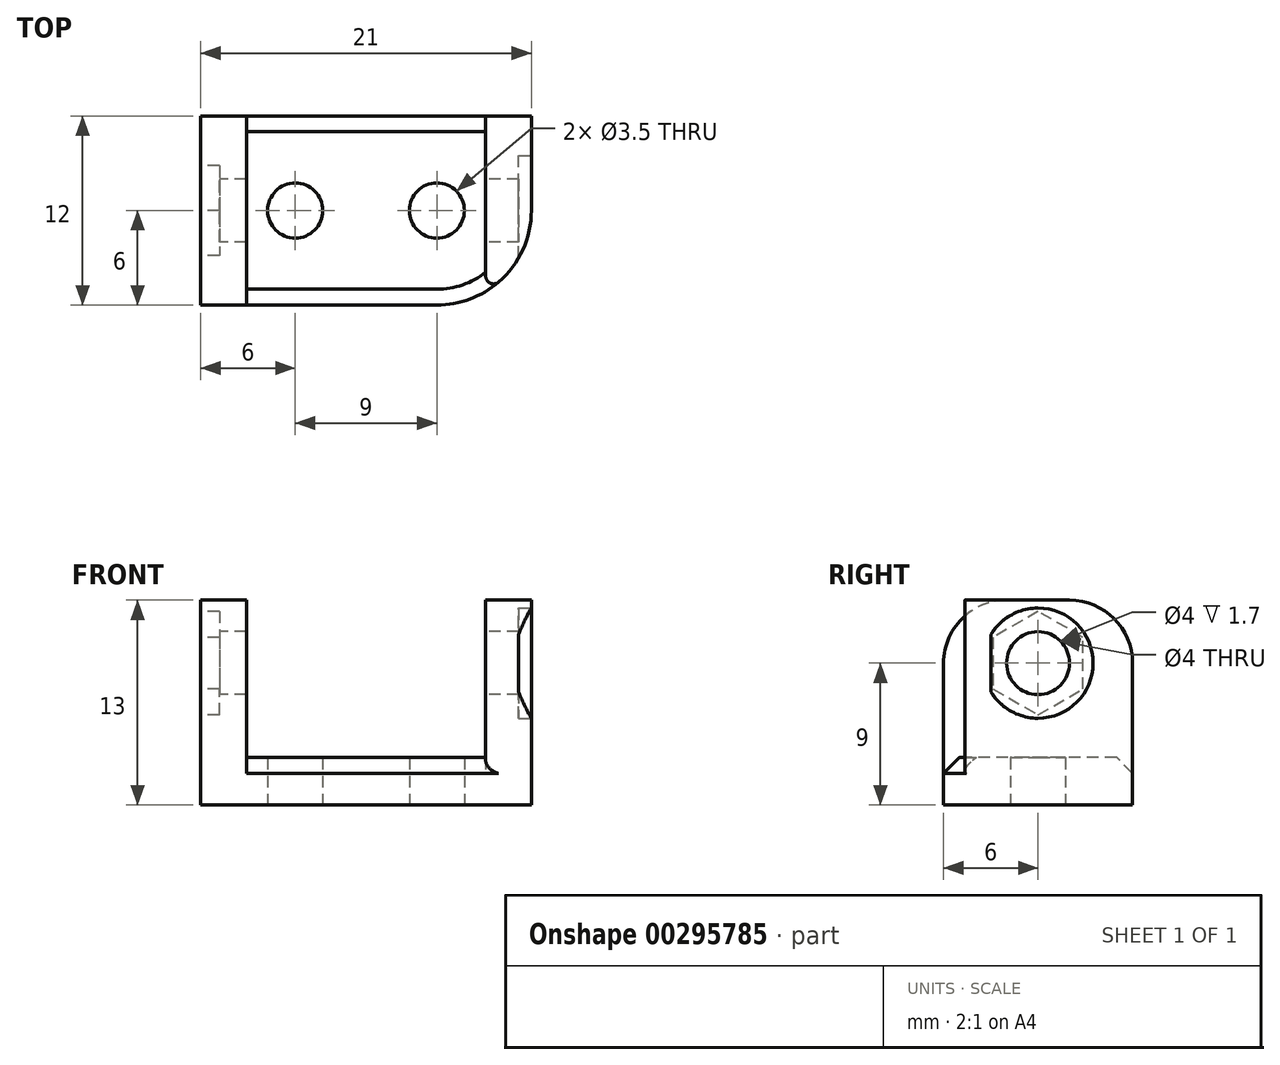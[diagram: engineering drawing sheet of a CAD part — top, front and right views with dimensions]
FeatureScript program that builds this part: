
annotation { "Feature Type Name" : "Feature", "Feature Type Description" : "" }
export const myFeature = defineFeature(function(context is Context, id is Id, definition is map)
    precondition{}
    {
        {
            var Q0;
            Q0=qCreatedBy(makeId("Top.planeOp"),FACE);
            var sketch = newSketch(context, id + "F0", { "sketchPlane" : qUnion([Q0])});
            skLineSegment(sketch, "E0.bottom", {"start": v(0, 0) * mm, "end": v(21, 0) * mm});
            skLineSegment(sketch, "E0.top", {"start": v(0, 12) * mm, "end": v(21, 12) * mm});
            skLineSegment(sketch, "E0.left", {"start": v(0, 0) * mm, "end": v(0, 12) * mm});
            skLineSegment(sketch, "E0.right", {"start": v(21, 0) * mm, "end": v(21, 12) * mm});
            skCircle(sketch, "E1", {"center": v(6, 6) * mm, "radius": 1.75 * mm});
            skPoint(sketch, "E1.centerSnap0", {"position": v(0, 6) * mm});
            skCircle(sketch, "E2", {"center": v(15, 6) * mm, "radius": 1.75 * mm});
            skSolve(sketch);
        }
        {
            var Q0;
            Q0 = qSketchRegion(id + "F0", true);
            extrude(context, id + "F1", {"entities" : qUnion([Q0]), "depth" : 3 * mm});
        }
        {
            var Q0;
            Q0=makeQuery(id+"F1.opExtrude","CAP_FACE",FACE,{"disambiguationData":[OSD([sQuery(id+"F0.wireOp",EDGE,"E0.bottom"),sQuery(id+"F0.wireOp",EDGE,"E0.top"),sQuery(id+"F0.wireOp",EDGE,"E0.left"),sQuery(id+"F0.wireOp",EDGE,"E0.right"),sQuery(id+"F0.wireOp",EDGE,"E1"),sQuery(id+"F0.wireOp",EDGE,"E2")])],"isStart":false});
            var sketch = newSketch(context, id + "F2", { "sketchPlane" : qUnion([Q0])});
            skLineSegment(sketch, "E3.bottom", {"start": v(0, 12) * mm, "end": v(2.9, 12) * mm});
            skLineSegment(sketch, "E3.top", {"start": v(0, 0) * mm, "end": v(2.9, 0) * mm});
            skLineSegment(sketch, "E3.left", {"start": v(0, 12) * mm, "end": v(0, 0) * mm});
            skLineSegment(sketch, "E3.right", {"start": v(2.9, 12) * mm, "end": v(2.9, 0) * mm});
            skLineSegment(sketch, "E4.bottom", {"start": v(21, 12) * mm, "end": v(18.1, 12) * mm});
            skLineSegment(sketch, "E4.top", {"start": v(21, 0) * mm, "end": v(18.1, 0) * mm});
            skLineSegment(sketch, "E4.left", {"start": v(21, 12) * mm, "end": v(21, 0) * mm});
            skLineSegment(sketch, "E4.right", {"start": v(18.1, 12) * mm, "end": v(18.1, 0) * mm});
            skSolve(sketch);
        }
        {
            var Q0;
            Q0 = qSketchRegion(id + "F2", true);
            extrude(context, id + "F3", {"entities" : qUnion([Q0]), "operationType" : NewBodyOperationType.ADD, "depth" : 10 * mm});
        }
        {
            var Q0;
            Q0=makeQuery(id+"F3.boolean.opBoolean","MERGE",FACE,{"derivedFrom":[makeQuery(id+"F1.opExtrude","SWEPT_FACE",FACE,{"disambiguationData":[OSD([sQuery(id+"F0.wireOp",EDGE,"E0.left")])]}),makeQuery(id+"F3.opExtrude","SWEPT_FACE",FACE,{"disambiguationData":[OSD([sQuery(id+"F2.wireOp",EDGE,"E3.left")])]})]});
            var sketch = newSketch(context, id + "F4", { "sketchPlane" : qUnion([Q0])});
            skCircle(sketch, "E5", {"center": v(-6, 9) * mm, "radius": 2 * mm});
            skPoint(sketch, "E5.centerSnap0", {"position": v(-6, 13) * mm});
            skSolve(sketch);
        }
        {
            var Q0;
            Q0 = qSketchRegion(id + "F4", true);
            extrude(context, id + "F5", {"entities" : qUnion([Q0]), "operationType" : NewBodyOperationType.REMOVE, "endBound" : BoundingType.THROUGH_ALL, "oppositeDirection" : true, "depth" : 25 * mm});
        }
        {
            var Q0;
            Q0=makeQuery(id+"F3.boolean.opBoolean","MERGE",EDGE,{"derivedFrom":[makeQuery(id+"F1.opExtrude","SWEPT_EDGE",EDGE,{"disambiguationData":[OSD([sQuery(id+"F0.wireOp",EDGE,"E0.bottom"),sQuery(id+"F0.wireOp",EDGE,"E0.right")])]}),makeQuery(id+"F3.opExtrude","SWEPT_EDGE",EDGE,{"disambiguationData":[OSD([sQuery(id+"F2.wireOp",EDGE,"E4.top"),sQuery(id+"F2.wireOp",EDGE,"E4.left")])]})]});
            fillet(context, id + "F6", {"entities" : qUnion([Q0]), "radius" : 6 * mm, "tangentPropagation" : true, "allowEdgeOverflow" : false});
        }
        {
            var Q0;
            Q0=makeQuery(id+"F1.opExtrude","CAP_EDGE",EDGE,{"disambiguationData":[OSD([sQuery(id+"F0.wireOp",EDGE,"E0.bottom")])],"isStart":false});
            var Q1;
            Q1=makeQuery(id+"F1.opExtrude","CAP_EDGE",EDGE,{"disambiguationData":[OSD([sQuery(id+"F0.wireOp",EDGE,"E0.top")])],"isStart":false});
            chamfer(context, id + "F7", {"entities" : qUnion([Q0, Q1]), "width" : 1 * mm, "tangentPropagation" : true});
        }
        {
            var Q0;
            Q0=makeQuery(id+"F3.opExtrude","CAP_EDGE",EDGE,{"disambiguationData":[OSD([sQuery(id+"F2.wireOp",EDGE,"E4.bottom")])],"isStart":false});
            var Q1;
            Q1=makeQuery(id+"F3.opExtrude","CAP_EDGE",EDGE,{"disambiguationData":[OSD([sQuery(id+"F2.wireOp",EDGE,"E3.top")])],"isStart":false});
            var Q2;
            Q2=makeQuery(id+"F3.opExtrude","CAP_EDGE",EDGE,{"disambiguationData":[OSD([sQuery(id+"F2.wireOp",EDGE,"E3.bottom")])],"isStart":false});
            fillet(context, id + "F8", {"entities" : qUnion([Q0, Q1, Q2]), "radius" : 4 * mm, "tangentPropagation" : true, "allowEdgeOverflow" : false});
        }
        {
            var Q0;
            Q0=makeQuery(id+"F6.opFillet","BLEND_EDGE",EDGE,{"blendedFrom":[makeQuery(id+"F3.boolean.opBoolean","MERGE",EDGE,{"derivedFrom":[makeQuery(id+"F1.opExtrude","SWEPT_EDGE",EDGE,{"disambiguationData":[OSD([sQuery(id+"F0.wireOp",EDGE,"E0.bottom"),sQuery(id+"F0.wireOp",EDGE,"E0.right")])]}),makeQuery(id+"F3.opExtrude","SWEPT_EDGE",EDGE,{"disambiguationData":[OSD([sQuery(id+"F2.wireOp",EDGE,"E4.top"),sQuery(id+"F2.wireOp",EDGE,"E4.left")])]})]}),makeQuery(id+"F3.opExtrude","SWEPT_FACE",FACE,{"disambiguationData":[OSD([sQuery(id+"F2.wireOp",EDGE,"E4.right")])]})],"blendedInto":[makeQuery(id+"F3.opExtrude","SWEPT_FACE",FACE,{"disambiguationData":[OSD([sQuery(id+"F2.wireOp",EDGE,"E4.right")])]})]});
            fillet(context, id + "F9", {"entities" : qUnion([Q0]), "radius" : .5 * mm, "tangentPropagation" : true, "allowEdgeOverflow" : false});
        }
        {
            var Q0;
            Q0=makeQuery(id+"F3.boolean.opBoolean","MERGE",FACE,{"derivedFrom":[makeQuery(id+"F1.opExtrude","SWEPT_FACE",FACE,{"disambiguationData":[OSD([sQuery(id+"F0.wireOp",EDGE,"E0.right")])]}),makeQuery(id+"F3.opExtrude","SWEPT_FACE",FACE,{"disambiguationData":[OSD([sQuery(id+"F2.wireOp",EDGE,"E4.left")])]})]});
            var sketch = newSketch(context, id + "F10", { "sketchPlane" : qUnion([Q0])});
            skArc(sketch, "E6.0", {"start": v(6, 11) * mm, "mid": v(8, 9) * mm, "end": v(6, 7) * mm, "construction": true});
            skCircle(sketch, "E7", {"center": v(6, 9) * mm, "radius": 3.5 * mm});
            skSolve(sketch);
        }
        {
            var Q0;
            Q0 = qSketchRegion(id + "F10", true);
            extrude(context, id + "F11", {"entities" : qUnion([Q0]), "operationType" : NewBodyOperationType.REMOVE, "oppositeDirection" : true, "depth" : .8 * mm});
        }
        {
            var Q0;
            Q0=makeQuery(id+"F3.boolean.opBoolean","MERGE",FACE,{"derivedFrom":[makeQuery(id+"F1.opExtrude","SWEPT_FACE",FACE,{"disambiguationData":[OSD([sQuery(id+"F0.wireOp",EDGE,"E0.left")])]}),makeQuery(id+"F3.opExtrude","SWEPT_FACE",FACE,{"disambiguationData":[OSD([sQuery(id+"F2.wireOp",EDGE,"E3.left")])]})]});
            var sketch = newSketch(context, id + "F12", { "sketchPlane" : qUnion([Q0])});
            skCircle(sketch, "E8.0", {"center": v(-6, 9) * mm, "radius": 2 * mm, "construction": true});
            skCircle(sketch, "E9.cCircle", {"center": v(-6, 9) * mm, "radius": 2.85 * mm, "construction": true});
            skLineSegment(sketch, "E9.0", {"start": v(-3.15, 10.65) * mm, "end": v(-3.15, 7.35) * mm});
            skLineSegment(sketch, "E9.1", {"start": v(-3.15, 7.35) * mm, "end": v(-6, 5.7) * mm});
            skLineSegment(sketch, "E9.2", {"start": v(-6, 5.7) * mm, "end": v(-8.85, 7.35) * mm});
            skLineSegment(sketch, "E9.3", {"start": v(-8.85, 7.35) * mm, "end": v(-8.85, 10.65) * mm});
            skLineSegment(sketch, "E9.4", {"start": v(-8.85, 10.65) * mm, "end": v(-6, 12.3) * mm});
            skLineSegment(sketch, "E9.5", {"start": v(-6, 12.3) * mm, "end": v(-3.15, 10.65) * mm});
            skPoint(sketch, "E9.0.midPoint", {"position": v(-3.15, 9) * mm});
            skSolve(sketch);
        }
        {
            var Q0;
            Q0 = qSketchRegion(id + "F12", true);
            extrude(context, id + "F13", {"entities" : qUnion([Q0]), "operationType" : NewBodyOperationType.REMOVE, "oppositeDirection" : true, "depth" : 1.2 * mm});
        }
    });
